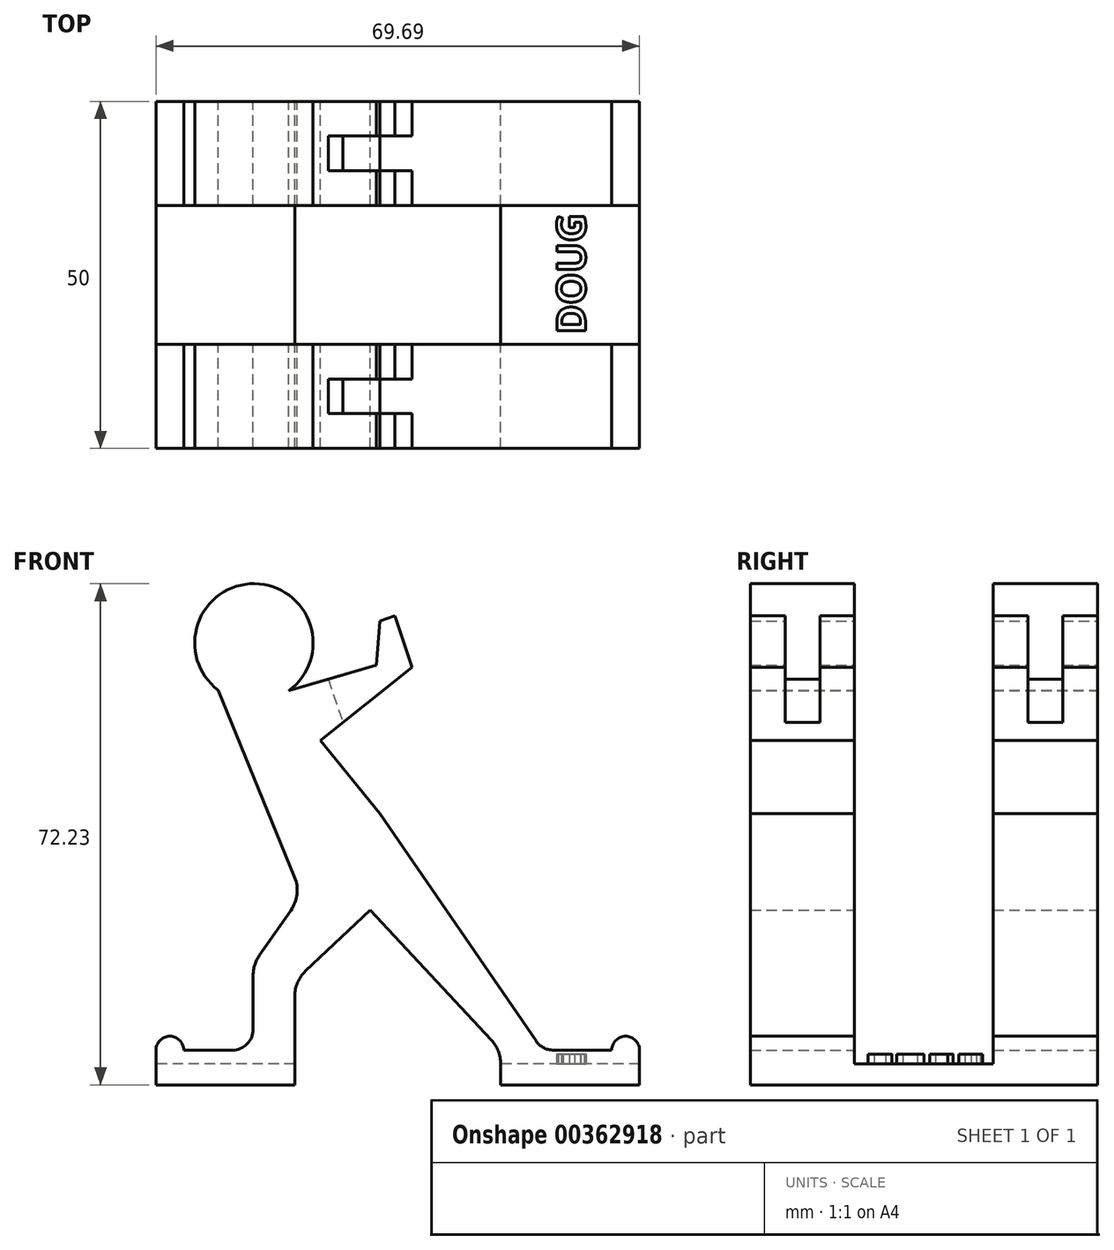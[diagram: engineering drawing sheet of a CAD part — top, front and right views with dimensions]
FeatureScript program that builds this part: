
annotation { "Feature Type Name" : "Feature", "Feature Type Description" : "" }
export const myFeature = defineFeature(function(context is Context, id is Id, definition is map)
    precondition{}
    {
        {
            var Q0;
            Q0=qCreatedBy(makeId("Front.planeOp"),FACE);
            var sketch = newSketch(context, id + "F0", { "sketchPlane" : qUnion([Q0])});
            skLineSegment(sketch, "E0", {"start": v(62.4, 5) * mm, "end": v(38.95, 39.06) * mm});
            skLineSegment(sketch, "E1", {"start": v(38.95, 39.06) * mm, "end": v(30.43, 49.64) * mm});
            skLineSegment(sketch, "E2", {"start": v(43.62, 60.2) * mm, "end": v(41.12, 67.6) * mm});
            skLineSegment(sketch, "E3", {"start": v(41.12, 67.6) * mm, "end": v(38.95, 66.86) * mm});
            skLineSegment(sketch, "E4", {"start": v(38.95, 66.86) * mm, "end": v(38.5, 60.5) * mm});
            skLineSegment(sketch, "E5", {"start": v(15.66, 56.9) * mm, "end": v(26.69, 29.94) * mm});
            skLineSegment(sketch, "E6", {"start": v(20.71, 5) * mm, "end": v(10.71, 5) * mm});
            skLineSegment(sketch, "E7", {"start": v(6.71, 5) * mm, "end": v(6.71, 0) * mm});
            skLineSegment(sketch, "E8", {"start": v(6.71, 0) * mm, "end": v(26.71, 0) * mm});
            skLineSegment(sketch, "E9", {"start": v(37.56, 25.18) * mm, "end": v(56.4, 5) * mm});
            skLineSegment(sketch, "E10", {"start": v(56.4, 5) * mm, "end": v(56.4, 0) * mm});
            skArc(sketch, "E11", {"start": v(25.86, 56.8) * mm, "mid": v(20.9, 72.23) * mm, "end": v(15.66, 56.9) * mm});
            skLineSegment(sketch, "E12", {"start": v(20.71, 5) * mm, "end": v(20.71, 17.35) * mm});
            skLineSegment(sketch, "E13", {"start": v(20.71, 17.35) * mm, "end": v(26.16, 25.15) * mm});
            skLineSegment(sketch, "E14", {"start": v(26.71, 0) * mm, "end": v(26.71, 14.93) * mm});
            skLineSegment(sketch, "E15", {"start": v(26.71, 14.93) * mm, "end": v(37.56, 25.18) * mm});
            skPoint(sketch, "E16.visualSharp", {"position": v(37.56, 25.18) * mm});
            skPoint(sketch, "E17.visualSharp", {"position": v(27.73, 27.4) * mm});
            skArc(sketch, "E17.filletArc", {"start": v(26.16, 25.15) * mm, "mid": v(27.03, 27.48) * mm, "end": v(26.69, 29.94) * mm});
            skLineSegment(sketch, "E18", {"start": v(43.62, 60.2) * mm, "end": v(30.43, 49.64) * mm});
            skPoint(sketch, "E19.orphan", {"position": v(27.73, 52.99) * mm});
            skLineSegment(sketch, "E20", {"start": v(38.5, 60.5) * mm, "end": v(25.86, 56.8) * mm});
            skLineSegment(sketch, "E21", {"start": v(25.86, 56.8) * mm, "end": v(25.86, 56.8) * mm});
            skLineSegment(sketch, "E22", {"start": v(62.4, 5) * mm, "end": v(72.4, 5) * mm});
            skLineSegment(sketch, "E23", {"start": v(56.4, 0) * mm, "end": v(76.4, 0) * mm});
            skLineSegment(sketch, "E24", {"start": v(76.4, 5) * mm, "end": v(76.4, 0) * mm});
            skArc(sketch, "E25", {"start": v(76.4, 5) * mm, "mid": v(74.4, 7) * mm, "end": v(72.4, 5) * mm});
            skArc(sketch, "E26", {"start": v(10.71, 5) * mm, "mid": v(8.71, 7) * mm, "end": v(6.71, 5) * mm});
            skSolve(sketch);
        }
        {
            var Q0;
            Q0=makeQuery(id+"F0.imprint","IMPRINT",FACE,{"disambiguationData":[TD([[makeQuery(id+"F0.imprint","IMPRINT",EDGE,{"derivedFrom":sQuery(id+"F0.wireOp",EDGE,"E0")}),1.0]])]});
            extrude(context, id + "F1", {"entities" : qUnion([Q0]), "depth" : 50 * mm});
        }
        {
            var Q0;
            Q0=makeQuery(id+"F1.opExtrude","SWEPT_EDGE",EDGE,{"disambiguationData":[OSD([sQuery(id+"F0.wireOp",EDGE,"E6"),sQuery(id+"F0.wireOp",EDGE,"E12")])]});
            fillet(context, id + "F2", {"entities" : qUnion([Q0]), "radius" : 3 * mm, "tangentPropagation" : true, "allowEdgeOverflow" : false});
        }
        {
            var Q0;
            Q0=makeQuery(id+"F1.opExtrude","SWEPT_EDGE",EDGE,{"disambiguationData":[OSD([sQuery(id+"F0.wireOp",EDGE,"E9"),sQuery(id+"F0.wireOp",EDGE,"E10")])]});
            var Q1;
            Q1=makeQuery(id+"F1.opExtrude","SWEPT_EDGE",EDGE,{"disambiguationData":[OSD([sQuery(id+"F0.wireOp",EDGE,"E14"),sQuery(id+"F0.wireOp",EDGE,"E15")])]});
            var Q2;
            Q2=makeQuery(id+"F1.opExtrude","SWEPT_EDGE",EDGE,{"disambiguationData":[OSD([sQuery(id+"F0.wireOp",EDGE,"E12"),sQuery(id+"F0.wireOp",EDGE,"E13")])]});
            fillet(context, id + "F3", {"entities" : qUnion([Q0, Q1, Q2]), "radius" : 5 * mm, "tangentPropagation" : true, "allowEdgeOverflow" : false});
        }
        {
            var Q0;
            Q0=qCreatedBy(makeId("Right.planeOp"),FACE);
            var sketch = newSketch(context, id + "F4", { "sketchPlane" : qUnion([Q0])});
            skLineSegment(sketch, "E27.bottom", {"start": v(-15, 3) * mm, "end": v(-35, 3) * mm});
            skLineSegment(sketch, "E27.top", {"start": v(-15, 87.35) * mm, "end": v(-35, 87.35) * mm});
            skLineSegment(sketch, "E27.left", {"start": v(-15, 3) * mm, "end": v(-15, 87.35) * mm});
            skLineSegment(sketch, "E27.right", {"start": v(-35, 3) * mm, "end": v(-35, 87.35) * mm});
            skSolve(sketch);
        }
        {
            var Q0;
            Q0 = qSketchRegion(id + "F4", true);
            extrude(context, id + "F5", {"entities" : qUnion([Q0]), "operationType" : NewBodyOperationType.REMOVE, "depth" : 82.2 * mm});
        }
        {
            var Q0;
            {var subQ2=sQuery(id+"F0.wireOp",EDGE,"E2");Q0=makeQuery(id+"F5.boolean.opBoolean","SPLIT",FACE,{"disambiguationData":[TD([makeQuery(id+"F5.opExtrude","SWEPT_FACE",FACE,{"disambiguationData":[OSD([sQuery(id+"F4.wireOp",EDGE,"E27.right")])]})])],"derivedFrom":makeQuery(id+"F1.opExtrude","SWEPT_FACE",FACE,{"disambiguationData":[OSD([subQ2])]})});}
            var sketch = newSketch(context, id + "F6", { "sketchPlane" : qUnion([Q0])});
            skLineSegment(sketch, "E28.bottom", {"start": v(-45, 51.74) * mm, "end": v(-40, 51.74) * mm});
            skLineSegment(sketch, "E28.top", {"start": v(-45, 28.32) * mm, "end": v(-40, 28.32) * mm});
            skLineSegment(sketch, "E28.left", {"start": v(-45, 51.74) * mm, "end": v(-45, 28.32) * mm});
            skLineSegment(sketch, "E28.right", {"start": v(-40, 51.74) * mm, "end": v(-40, 28.32) * mm});
            skPoint(sketch, "E29.oppositeSnap0", {"position": v(-42.5, 51.74) * mm});
            skPoint(sketch, "E30", {"position": v(-42.5, 50.87) * mm});
            skSolve(sketch);
        }
        {
            var Q0;
            {var subQ0=sQuery(id+"F6.wireOp",EDGE,"E28.left");var subQ2=sQuery(id+"F0.wireOp",EDGE,"E3");var subQ3=sQuery(id+"F0.wireOp",EDGE,"E2");var subQ6=makeQuery(id+"F5.opExtrude","SWEPT_FACE",FACE,{"disambiguationData":[OSD([sQuery(id+"F4.wireOp",EDGE,"E27.right")])]});var subQ7=makeQuery(id+"F5.boolean.opBoolean","SPLIT",EDGE,{"disambiguationData":[TD([subQ6])],"derivedFrom":makeQuery(id+"F1.opExtrude","SWEPT_EDGE",EDGE,{"disambiguationData":[OSD([subQ3,subQ2])]})});var subQ8=makeQuery(id+"F6.imprint","INTERSECT",VERTEX,{"derivedFrom":[subQ7,subQ0]});Q0=makeQuery(id+"F6.imprint","IMPRINT",FACE,{"disambiguationData":[TD([[makeQuery(id+"F6.imprint","IMPRINT",EDGE,{"disambiguationData":[TD([[subQ8,-1.0]])],"derivedFrom":subQ0}),1.0]])]});}
            var Q1;
            {var subQ0=sQuery(id+"F6.wireOp",EDGE,"E28.top");Q1=makeQuery(id+"F6.imprint","IMPRINT",FACE,{"disambiguationData":[TD([[makeQuery(id+"F6.imprint","IMPRINT",EDGE,{"derivedFrom":subQ0}),1.0]])]});}
            var Q2;
            {var subQ1=sQuery(id+"F6.wireOp",EDGE,"E28.bottom");var subQ10=makeQuery(id+"F6.imprint","IMPRINT",VERTEX,{"derivedFrom":subQ1});Q2=makeQuery(id+"F6.imprint","IMPRINT",FACE,{"disambiguationData":[TD([[makeQuery(id+"F6.imprint","IMPRINT",EDGE,{"disambiguationData":[TD([[subQ10,1.0]])],"derivedFrom":subQ1}),-1.0]])]});}
            extrude(context, id + "F7", {"entities" : qUnion([Q0, Q1, Q2]), "operationType" : NewBodyOperationType.REMOVE, "oppositeDirection" : true, "depth" : 12 * mm});
        }
        {
            var Q0;
            {var subQ2=sQuery(id+"F0.wireOp",EDGE,"E2");Q0=makeQuery(id+"F5.boolean.opBoolean","SPLIT",FACE,{"disambiguationData":[TD([makeQuery(id+"F5.opExtrude","SWEPT_FACE",FACE,{"disambiguationData":[OSD([sQuery(id+"F4.wireOp",EDGE,"E27.left")])]})])],"derivedFrom":makeQuery(id+"F1.opExtrude","SWEPT_FACE",FACE,{"disambiguationData":[OSD([subQ2])]})});}
            var sketch = newSketch(context, id + "F8", { "sketchPlane" : qUnion([Q0])});
            skLineSegment(sketch, "E31.bottom", {"start": v(-10, 51.2) * mm, "end": v(-5, 51.2) * mm});
            skLineSegment(sketch, "E31.top", {"start": v(-10, 29.26) * mm, "end": v(-5, 29.26) * mm});
            skLineSegment(sketch, "E31.left", {"start": v(-10, 51.2) * mm, "end": v(-10, 29.26) * mm});
            skLineSegment(sketch, "E31.right", {"start": v(-5, 51.2) * mm, "end": v(-5, 29.26) * mm});
            skSolve(sketch);
        }
        {
            var Q0;
            {var subQ0=sQuery(id+"F8.wireOp",EDGE,"E31.top");Q0=makeQuery(id+"F8.imprint","IMPRINT",FACE,{"disambiguationData":[TD([[makeQuery(id+"F8.imprint","IMPRINT",EDGE,{"derivedFrom":subQ0}),1.0]])]});}
            var Q1;
            {var subQ0=sQuery(id+"F8.wireOp",EDGE,"E31.left");var subQ2=sQuery(id+"F0.wireOp",EDGE,"E3");var subQ3=sQuery(id+"F0.wireOp",EDGE,"E2");var subQ6=makeQuery(id+"F5.opExtrude","SWEPT_FACE",FACE,{"disambiguationData":[OSD([sQuery(id+"F4.wireOp",EDGE,"E27.left")])]});var subQ7=makeQuery(id+"F5.boolean.opBoolean","SPLIT",EDGE,{"disambiguationData":[TD([subQ6])],"derivedFrom":makeQuery(id+"F1.opExtrude","SWEPT_EDGE",EDGE,{"disambiguationData":[OSD([subQ3,subQ2])]})});var subQ8=makeQuery(id+"F8.imprint","INTERSECT",VERTEX,{"derivedFrom":[subQ7,subQ0]});Q1=makeQuery(id+"F8.imprint","IMPRINT",FACE,{"disambiguationData":[TD([[makeQuery(id+"F8.imprint","IMPRINT",EDGE,{"disambiguationData":[TD([[subQ8,-1.0]])],"derivedFrom":subQ0}),1.0]])]});}
            extrude(context, id + "F9", {"entities" : qUnion([Q0, Q1]), "operationType" : NewBodyOperationType.REMOVE, "oppositeDirection" : true, "depth" : 12 * mm});
        }
        {
            var Q0;
            {var subQ0=sQuery(id+"F0.wireOp",EDGE,"E22");var subQ1=sQuery(id+"F0.wireOp",EDGE,"E0");Q0=makeQuery(id+"F5.boolean.opBoolean","SPLIT",EDGE,{"disambiguationData":[TD([makeQuery(id+"F5.opExtrude","SWEPT_FACE",FACE,{"disambiguationData":[OSD([sQuery(id+"F4.wireOp",EDGE,"E27.right")])]})])],"derivedFrom":makeQuery(id+"F1.opExtrude","SWEPT_EDGE",EDGE,{"disambiguationData":[OSD([subQ1,subQ0])]})});}
            var Q1;
            {var subQ0=sQuery(id+"F0.wireOp",EDGE,"E22");var subQ1=sQuery(id+"F0.wireOp",EDGE,"E0");Q1=makeQuery(id+"F5.boolean.opBoolean","SPLIT",EDGE,{"disambiguationData":[TD([makeQuery(id+"F5.opExtrude","SWEPT_FACE",FACE,{"disambiguationData":[OSD([sQuery(id+"F4.wireOp",EDGE,"E27.left")])]})])],"derivedFrom":makeQuery(id+"F1.opExtrude","SWEPT_EDGE",EDGE,{"disambiguationData":[OSD([subQ1,subQ0])]})});}
            fillet(context, id + "F10", {"entities" : qUnion([Q0, Q1]), "radius" : 3 * mm, "tangentPropagation" : true, "allowEdgeOverflow" : false});
        }
        {
            var Q0;
            Q0=makeQuery(id+"F5.boolean.opBoolean","COPY",FACE,{"disambiguationData":[TD([makeQuery(id+"F1.opExtrude","SWEPT_FACE",FACE,{"disambiguationData":[OSD([sQuery(id+"F0.wireOp",EDGE,"E10")])]})])],"derivedFrom":makeQuery(id+"F5.opExtrude","SWEPT_FACE",FACE,{"disambiguationData":[OSD([sQuery(id+"F4.wireOp",EDGE,"E27.bottom")])]})});
            var sketch = newSketch(context, id + "F11", { "sketchPlane" : qUnion([Q0])});
            skText(sketch, "E32", { "text": "DOUG", "fontName": "OpenSans-Bold.ttf"});
            const initialGuessF11  = {"E32": [0.06862, -0.03358, 0, 1, 0.00417]};
            skSetInitialGuess(sketch, initialGuessF11);
            skSolve(sketch);
        }
        {
            var Q0;
            Q0 = qSketchRegion(id + "F11", true);
            extrude(context, id + "F12", {"entities" : qUnion([Q0]), "operationType" : NewBodyOperationType.ADD, "depth" : 1.4 * mm});
        }
    });
